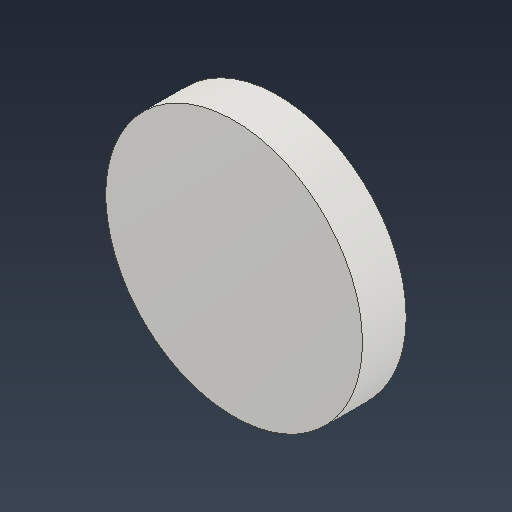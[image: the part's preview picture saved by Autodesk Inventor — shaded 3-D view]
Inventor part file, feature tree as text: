
AUTODESK INVENTOR PART (.ipt)
format: ipt  version: 2022 (Build 260153000, 153)  size: 145,408 bytes
history: native  units: mm (DEFAULTED — no unit token found)
features: plane x3, other x3, sketch x2, extrude x1
ambient origin geometry x8: Origin, YZ Plane, XZ Plane, XY Plane, X Axis, Y Axis, Z Axis, Center Point
bodies: Solid1 (feature_tree)
feature tree (9):
  extrude  "Extrusion1"  Depth=20.0mm TaperAngle=0.0deg
  plane  "Work Plane2"
  plane  "Work Plane8"
  plane  "Work Plane9"
  other  "Spur Gear"
  sketch  "Sketch1"  dims[d0=117.316266mm d1=20.0mm d2=0.0mm]
  sketch  "Sketch2"  dims[d3=121.316266mm d4=10.0mm d5=0.0mm d16=104.0mm d17=0.0mm d34=0.551157mm d39=0.0mm d41=0.0mm d43=104.0mm d46=104.0mm d47=0.0mm d48=0.0mm]
  other  "Srf1"
  other  "Pitch Diameter"
